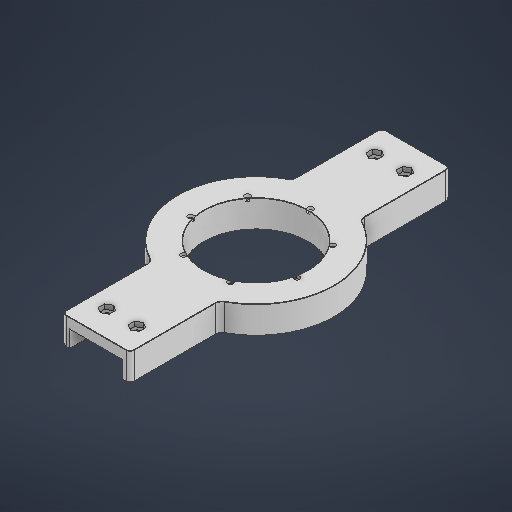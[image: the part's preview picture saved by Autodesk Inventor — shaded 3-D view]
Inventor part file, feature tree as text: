
AUTODESK INVENTOR PART (.ipt)
format: ipt  version: 2025 (Build 290162000, 162)  size: 470,016 bytes
history: native  units: in
note: dims shown in document units (in); Inventor stores cm internally (conversion verified against a paired STEP export)
features: sketch x6, extrude x4, hole x2, fillet x2, chamfer x1
ambient origin geometry x8: Origin, YZ Plane, XZ Plane, XY Plane, X Axis, Y Axis, Z Axis, Center Point
bodies: Solid1 (feature_tree)
feature tree (15):
  extrude  "Extrusion1"  Depth=4.5276in
  sketch  "Sketch2"  dims[d4=0.7874in d5=0.0in d6=3.1496in]
  hole  "Hole1"  [1 undecoded]
  extrude  "Extrusion3"  Depth=0.1594in
  fillet  "Fillet1"  Radius=2.7559in
  fillet  "Fillet2"  Radius=0.0787in
  chamfer  "Chamfer1"  Distance=0.0098in Angle=45.0deg
  extrude  "Extrusion4"  Depth=0.1358in
  hole  "Hole2"  [1 undecoded]
  extrude  "Extrusion5"  Depth=0.1358in
  sketch  "Sketch1"  dims[d0=3.002in d3=4.5276in]
  sketch  "Sketch Circular Pattern2"  dims[d14=0.0617in d15=0.1575in d16=0.1575in d17=0.0787in d18=90.0deg d19=0.248in d20=0.8108in d21=0.1594in d22=2.7559in d24=360.0deg d26=0.0787in d27=0.0in]
  sketch  "Sketch3"  dims[d28=0.1969in]
  sketch  "Sketch4"  dims[d29=0.1181in d30=0.0098in d31=0.0787in d32=45.0deg]
  sketch  "Sketch5"  dims[d35=1.5453in d37=1.1122in d38=1.1122in d39=1.5453in d40=0.1181in d41=0.1181in d42=0.1181in d43=0.4951in d44=0.0in d45=0.748in d48=0.748in d50=0.0935in d51=0.0935in d52=1.7323in d53=1.5453in d55=0.0935in d56=0.0935in d57=0.748in d58=0.748in d59=0.8661in d60=0.8661in d61=0.3396in d62=0.3396in d63=0.1276in d64=0.315in d65=0.1575in d66=0.0787in d67=90.0deg d68=0.315in d69=0.8108in d70=0.3248in d71=0.3248in d72=0.3248in d73=0.3248in d74=0.1358in d75=0.0in d76=1.9685in d77=2.2638in d78=2.2638in d79=2.5874in d80=2.5874in d81=1.9685in d46=0.0344in]
note: 2 required parameter values undecoded (feature->parameter linkage not recoverable at this tier; creation-order binding heuristic only, values carry confidence <= 0.55)
